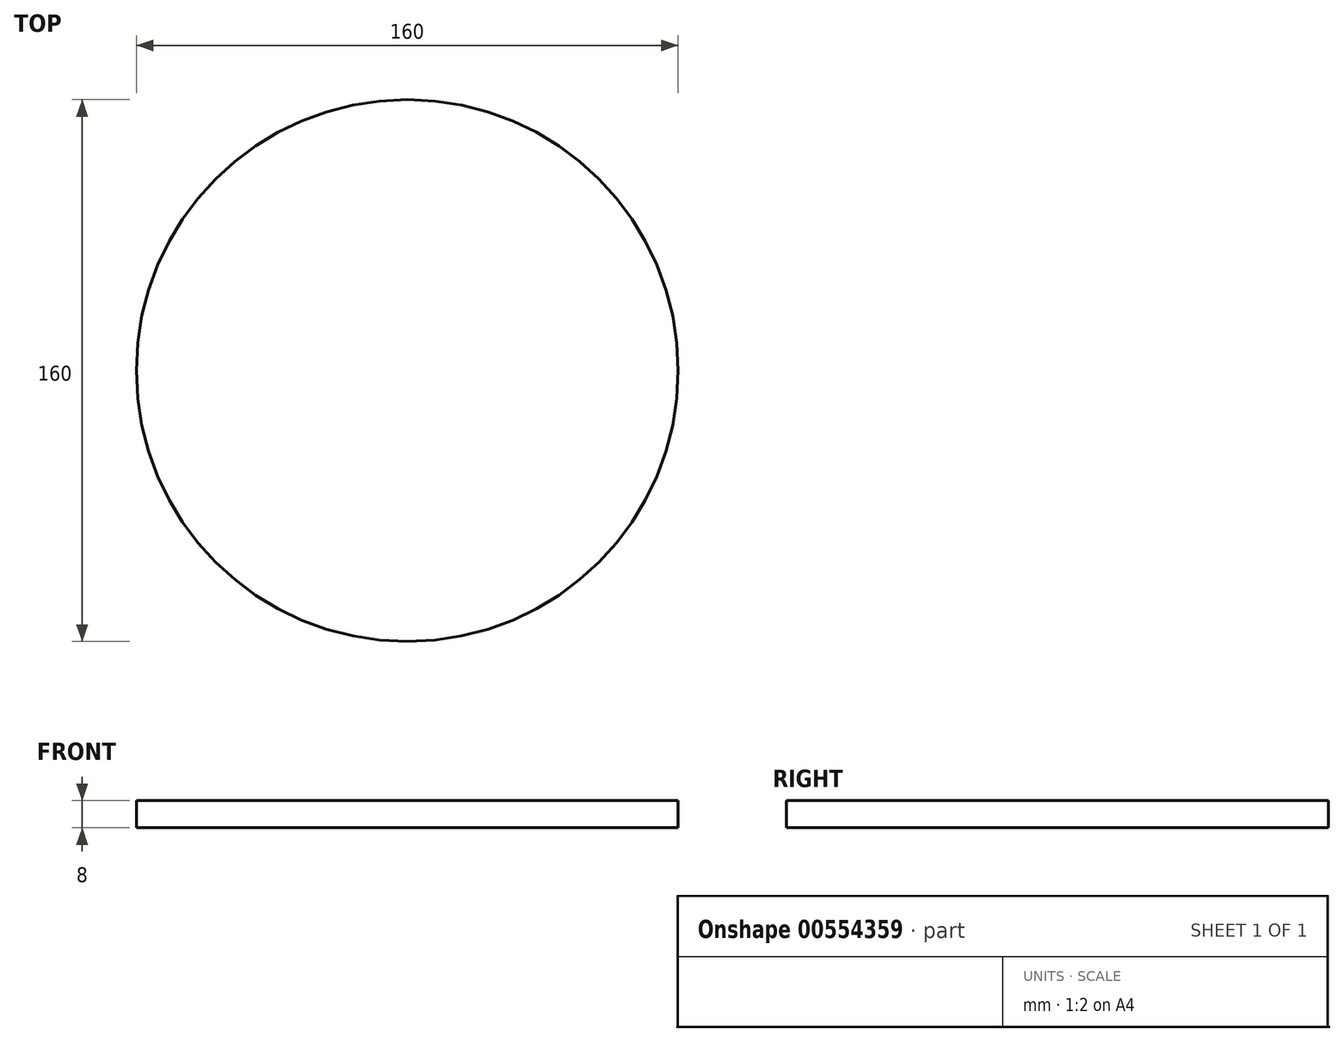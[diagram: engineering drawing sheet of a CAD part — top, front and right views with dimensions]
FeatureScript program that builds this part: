
annotation { "Feature Type Name" : "Feature", "Feature Type Description" : "" }
export const myFeature = defineFeature(function(context is Context, id is Id, definition is map)
    precondition{}
    {
        {
            var Q0;
            Q0=qCreatedBy(makeId("Top.planeOp"),FACE);
            var sketch = newSketch(context, id + "F0", { "sketchPlane" : qUnion([Q0])});
            skCircle(sketch, "E0", {"center": v(0, 0) * mm, "radius": 80 * mm});
            skSolve(sketch);
        }
        {
            var Q0;
            Q0 = qSketchRegion(id + "F0", true);
            extrude(context, id + "F1", {"entities" : qUnion([Q0]), "depth" : 8 * mm, "offsetDistance" : 25 * mm});
        }
    });
